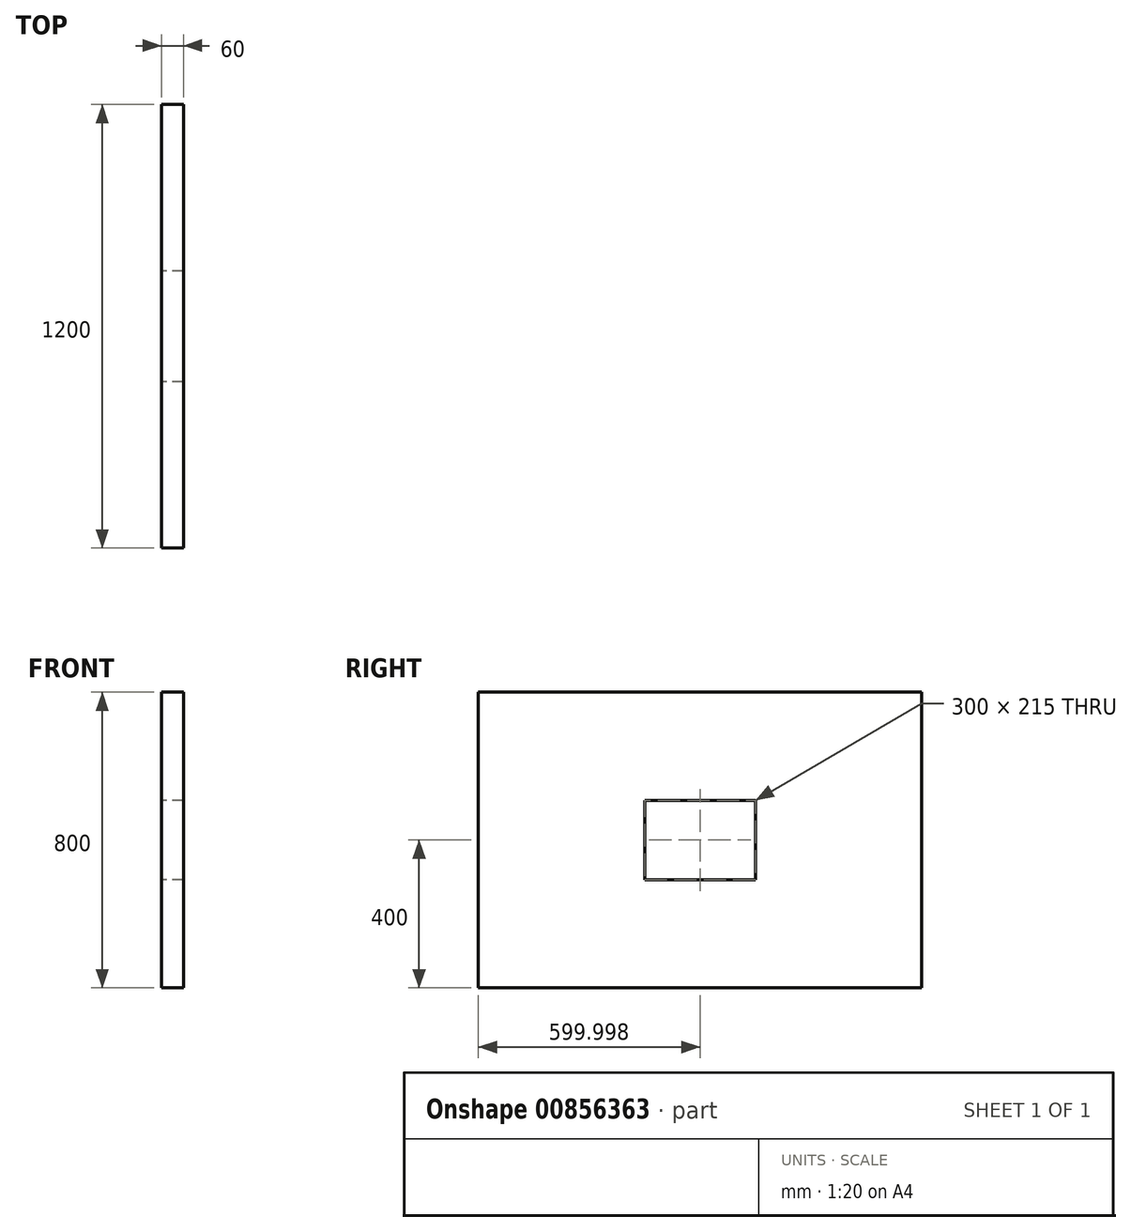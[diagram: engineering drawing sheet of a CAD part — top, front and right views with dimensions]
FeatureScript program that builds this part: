
annotation { "Feature Type Name" : "Feature", "Feature Type Description" : "" }
export const myFeature = defineFeature(function(context is Context, id is Id, definition is map)
    precondition{}
    {
        {
            var Q0;
            Q0=qCreatedBy(makeId("Right.planeOp"),FACE);
            var sketch = newSketch(context, id + "F0", { "sketchPlane" : qUnion([Q0])});
            skLineSegment(sketch, "E0.bottom", {"start": v(-816.37, 430.45) * mm, "end": v(383.63, 430.45) * mm});
            skLineSegment(sketch, "E0.top", {"start": v(-816.37, -369.55) * mm, "end": v(383.63, -369.55) * mm});
            skLineSegment(sketch, "E0.left", {"start": v(-816.37, 430.45) * mm, "end": v(-816.37, -369.55) * mm});
            skLineSegment(sketch, "E0.right", {"start": v(383.63, 430.45) * mm, "end": v(383.63, -369.55) * mm});
            skLineSegment(sketch, "E1.bottom", {"start": v(-66.37, -77.05) * mm, "end": v(-366.37, -77.05) * mm});
            skLineSegment(sketch, "E1.top", {"start": v(-66.37, 137.95) * mm, "end": v(-366.37, 137.95) * mm});
            skLineSegment(sketch, "E1.left", {"start": v(-66.37, -77.05) * mm, "end": v(-66.37, 137.95) * mm});
            skLineSegment(sketch, "E1.right", {"start": v(-366.37, -77.05) * mm, "end": v(-366.37, 137.95) * mm});
            skSolve(sketch);
        }
        {
            var Q0;
            Q0=makeQuery(id+"F0.imprint","IMPRINT",FACE,{"disambiguationData":[TD([[makeQuery(id+"F0.imprint","IMPRINT",EDGE,{"derivedFrom":sQuery(id+"F0.wireOp",EDGE,"E0.bottom")}),-1.0]])]});
            extrude(context, id + "F1", {"entities" : qUnion([Q0]), "depth" : 60 * mm, "offsetDistance" : 25.4 * mm});
        }
    });
